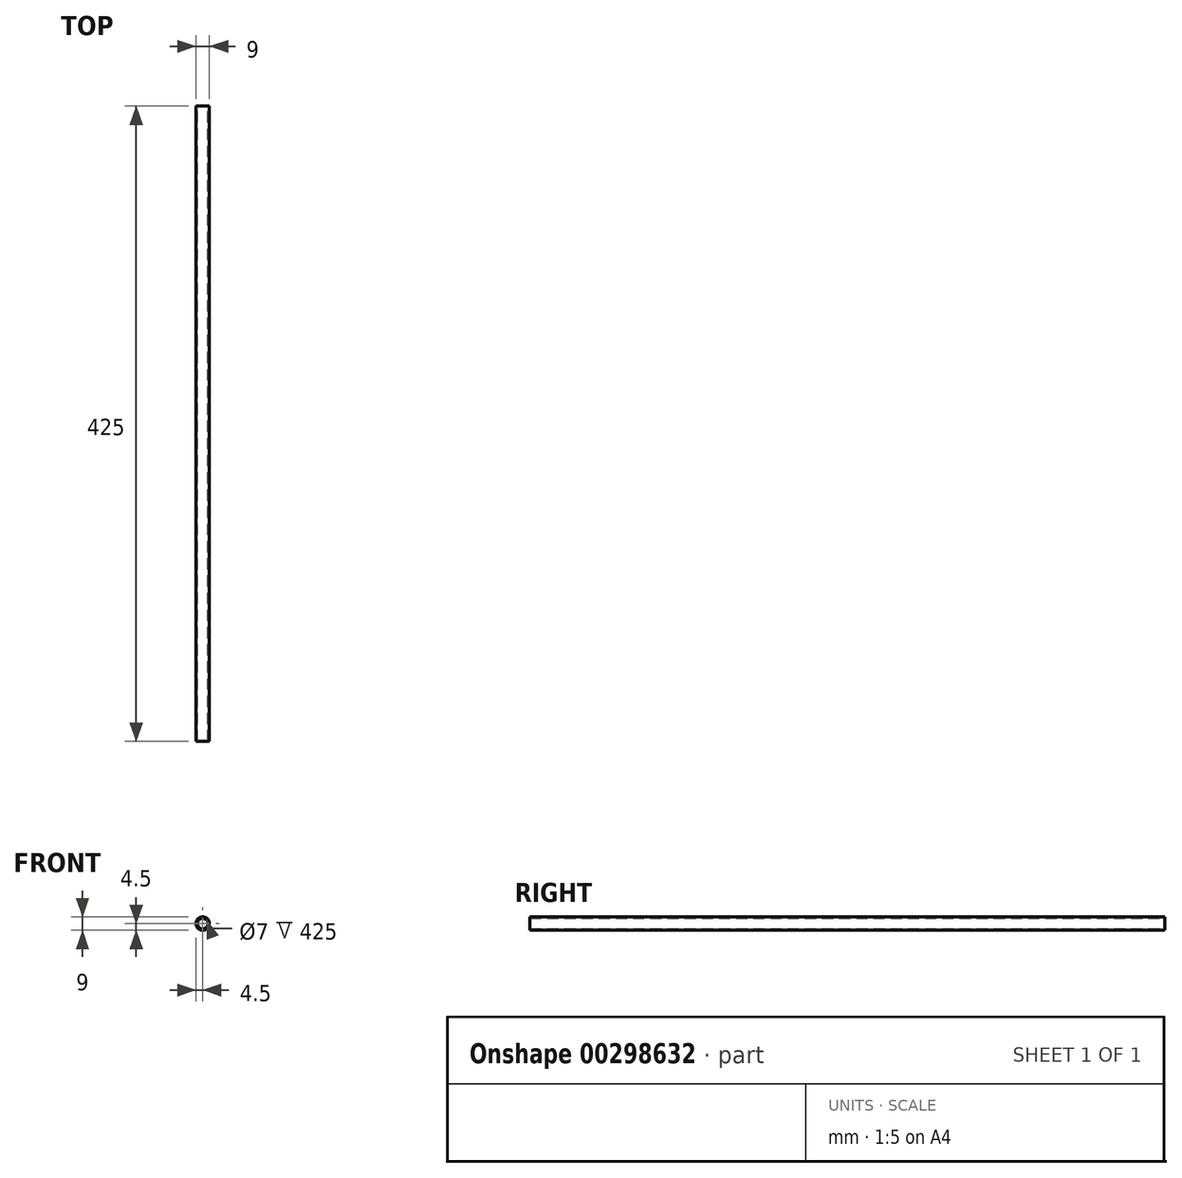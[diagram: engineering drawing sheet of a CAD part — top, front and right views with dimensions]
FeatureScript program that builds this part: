
annotation { "Feature Type Name" : "Feature", "Feature Type Description" : "" }
export const myFeature = defineFeature(function(context is Context, id is Id, definition is map)
    precondition{}
    {
        {
            var Q0;
            Q0=qCreatedBy(makeId("Front.planeOp"),FACE);
            var sketch = newSketch(context, id + "F0", { "sketchPlane" : qUnion([Q0])});
            skCircle(sketch, "E0", {"center": v(0, 0) * mm, "radius": 4.5 * mm});
            skCircle(sketch, "E1", {"center": v(0, 0) * mm, "radius": 3.5 * mm});
            skSolve(sketch);
        }
        {
            var Q0;
            Q0=makeQuery(id+"F0.imprint","IMPRINT",FACE,{"disambiguationData":[TD([[makeQuery(id+"F0.imprint","IMPRINT",EDGE,{"derivedFrom":sQuery(id+"F0.wireOp",EDGE,"E0")}),1.0]])]});
            extrude(context, id + "F1", {"entities" : qUnion([Q0]), "depth" : 425 * mm});
        }
    });
